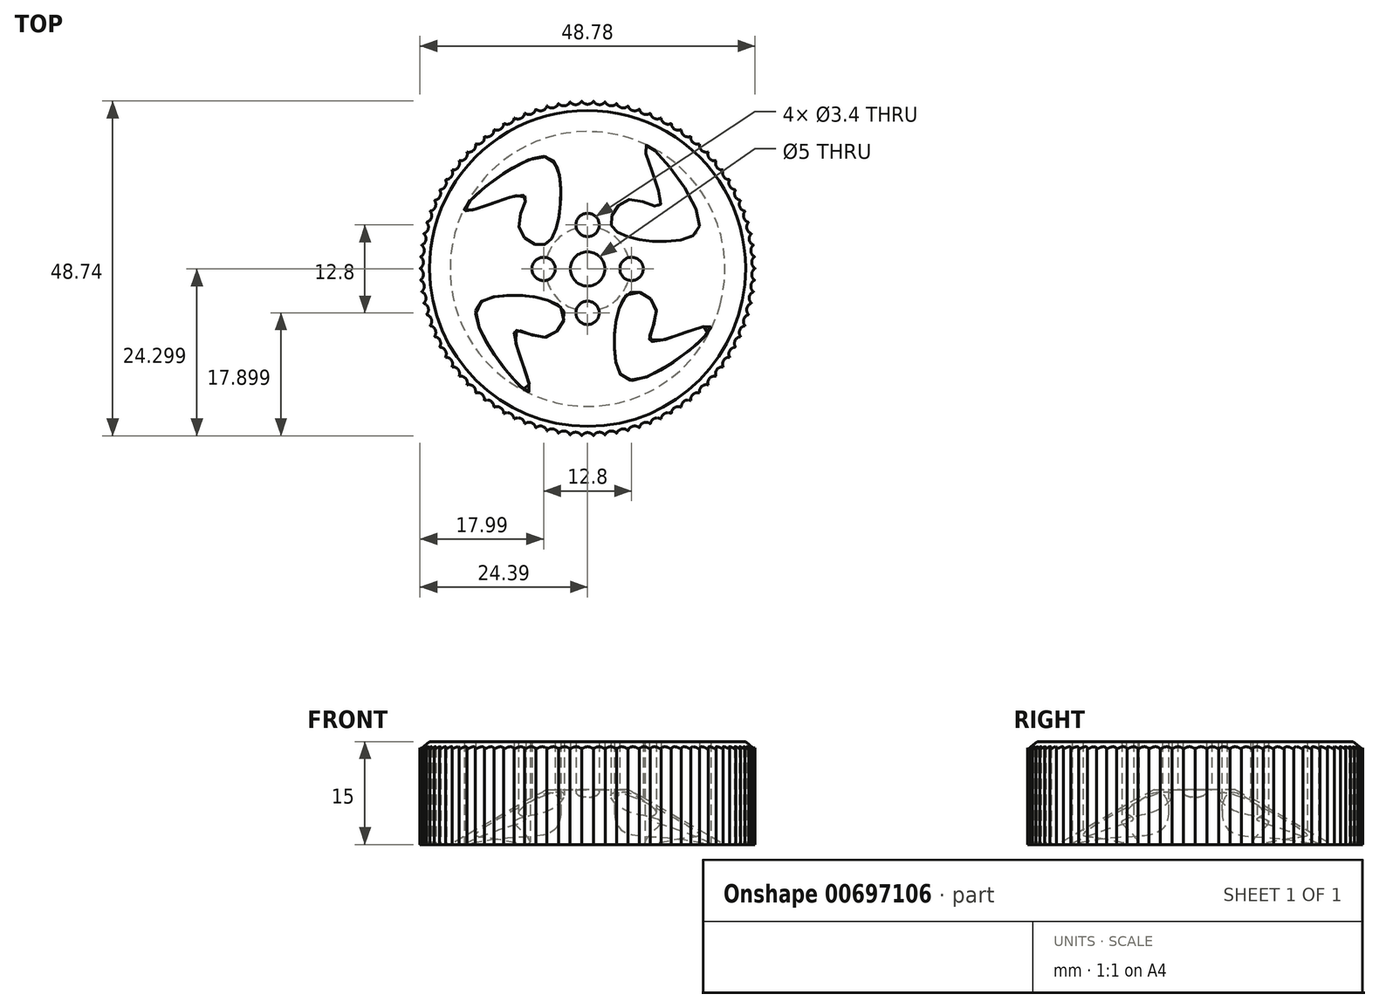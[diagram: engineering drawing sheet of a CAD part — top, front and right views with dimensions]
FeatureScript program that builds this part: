
annotation { "Feature Type Name" : "Feature", "Feature Type Description" : "" }
export const myFeature = defineFeature(function(context is Context, id is Id, definition is map)
    precondition{}
    {
        {
            var Q0;
            Q0=qCreatedBy(makeId("Top.planeOp"),FACE);
            var sketch = newSketch(context, id + "F0", { "sketchPlane" : qUnion([Q0])});
            skCircle(sketch, "E0", {"center": v(0, -0.07) * mm, "radius": 25 * mm});
            skCircle(sketch, "E1", {"center": v(0, -0.07) * mm, "radius": 20 * mm});
            skCircle(sketch, "E2", {"center": v(0, -0.07) * mm, "radius": 2.5 * mm});
            skCircle(sketch, "E3", {"center": v(0, 6.33) * mm, "radius": 1.7 * mm});
            skCircle(sketch, "E4", {"center": v(6.4, -0.07) * mm, "radius": 1.7 * mm});
            skCircle(sketch, "E5", {"center": v(0, -6.47) * mm, "radius": 1.7 * mm});
            skCircle(sketch, "E6", {"center": v(-6.4, -0.07) * mm, "radius": 1.7 * mm});
            skSolve(sketch);
        }
        {
            var Q0;
            Q0=makeQuery(id+"F0.imprint","IMPRINT",FACE,{"disambiguationData":[TD([[makeQuery(id+"F0.imprint","IMPRINT",EDGE,{"derivedFrom":sQuery(id+"F0.wireOp",EDGE,"E0")}),1.0]])]});
            var Q1;
            Q1=makeQuery(id+"F0.imprint","IMPRINT",FACE,{"disambiguationData":[TD([[makeQuery(id+"F0.imprint","IMPRINT",EDGE,{"derivedFrom":sQuery(id+"F0.wireOp",EDGE,"E1")}),1.0]])]});
            extrude(context, id + "F1", {"entities" : qUnion([Q0, Q1]), "depth" : 15 * mm, "offsetDistance" : 25 * mm});
        }
        {
            var Q0;
            Q0=makeQuery(id+"F0.imprint","IMPRINT",FACE,{"disambiguationData":[TD([[makeQuery(id+"F0.imprint","IMPRINT",EDGE,{"derivedFrom":sQuery(id+"F0.wireOp",EDGE,"E1")}),1.0]])]});
            var Q1;
            Q1=makeQuery(id+"F0.imprint","IMPRINT",FACE,{"disambiguationData":[TD([[makeQuery(id+"F0.imprint","IMPRINT",EDGE,{"derivedFrom":sQuery(id+"F0.wireOp",EDGE,"E5")}),1.0]])]});
            var Q2;
            Q2=makeQuery(id+"F0.imprint","IMPRINT",FACE,{"disambiguationData":[TD([[makeQuery(id+"F0.imprint","IMPRINT",EDGE,{"derivedFrom":sQuery(id+"F0.wireOp",EDGE,"E4")}),1.0]])]});
            var Q3;
            Q3=makeQuery(id+"F0.imprint","IMPRINT",FACE,{"disambiguationData":[TD([[makeQuery(id+"F0.imprint","IMPRINT",EDGE,{"derivedFrom":sQuery(id+"F0.wireOp",EDGE,"E2")}),1.0]])]});
            var Q4;
            Q4=makeQuery(id+"F0.imprint","IMPRINT",FACE,{"disambiguationData":[TD([[makeQuery(id+"F0.imprint","IMPRINT",EDGE,{"derivedFrom":sQuery(id+"F0.wireOp",EDGE,"E3")}),1.0]])]});
            var Q5;
            Q5=makeQuery(id+"F0.imprint","IMPRINT",FACE,{"disambiguationData":[TD([[makeQuery(id+"F0.imprint","IMPRINT",EDGE,{"derivedFrom":sQuery(id+"F0.wireOp",EDGE,"E6")}),1.0]])]});
            extrude(context, id + "F2", {"entities" : qUnion([Q0, Q1, Q2, Q3, Q4, Q5]), "operationType" : NewBodyOperationType.REMOVE, "depth" : 8 * mm, "offsetDistance" : 25 * mm, "hasDraft" : true, "draftAngle" : 60 * degree, "draftPullDirection" : true});
        }
        {
            var Q0;
            Q0=qCreatedBy(makeId("Top.planeOp"),FACE);
            var sketch = newSketch(context, id + "F3", { "sketchPlane" : qUnion([Q0])});
            skCircle(sketch, "E7", {"center": v(0, 24.9) * mm, "radius": 1 * mm});
            skSolve(sketch);
        }
        {
            var Q0;
            Q0=makeQuery(id+"F3.imprint","IMPRINT",FACE,{"disambiguationData":[TD([[makeQuery(id+"F3.imprint","IMPRINT",EDGE,{"derivedFrom":sQuery(id+"F3.wireOp",EDGE,"E7")}),1.0]])]});
            extrude(context, id + "F4", {"entities" : qUnion([Q0]), "depth" : 25 * mm, "offsetDistance" : 25 * mm});
        }
        {
            var Q0;
            Q0=qCreatedBy(makeId("Right.planeOp"),FACE);
            var sketch = newSketch(context, id + "F5", { "sketchPlane" : qUnion([Q0])});
            skLineSegment(sketch, "E8", {"start": v(0, 25.16) * mm, "end": v(0, -9.7) * mm});
            skSolve(sketch);
        }
        {
            var Q0;
            Q0=makeQuery(id+"F4.opExtrude","SWEPT_BODY",BODY,{"disambiguationData":[OSD([sQuery(id+"F3.wireOp",EDGE,"E7")])]});
            var Q1;
            Q1=sQuery(id+"F5.wireOp",EDGE,"E8");
            circularPattern(context, id + "F6", {"operationType" : NewBodyOperationType.REMOVE, "entities" : qUnion([Q0]), "axis" : qUnion([Q1]), "angle" : 360 * degree, "instanceCount" : 90, "equalSpace" : true});
        }
        {
            var Q0;
            Q0=makeQuery(id+"F1.opExtrude","CAP_FACE",FACE,{"disambiguationData":[OSD([sQuery(id+"F0.wireOp",EDGE,"E0"),sQuery(id+"F0.wireOp",EDGE,"E2"),sQuery(id+"F0.wireOp",EDGE,"E3"),sQuery(id+"F0.wireOp",EDGE,"E4"),sQuery(id+"F0.wireOp",EDGE,"E5"),sQuery(id+"F0.wireOp",EDGE,"E6")])],"isStart":false});
            var sketch = newSketch(context, id + "F7", { "sketchPlane" : qUnion([Q0])});
            skCircle(sketch, "E9", {"center": v(0, 0) * mm, "radius": 23 * mm});
            skCircle(sketch, "E10", {"center": v(0, 0) * mm, "radius": 25.5 * mm});
            skSolve(sketch);
        }
        {
            var Q0;
            Q0=makeQuery(id+"F7.imprint","IMPRINT",FACE,{"disambiguationData":[TD([[makeQuery(id+"F7.imprint","IMPRINT",EDGE,{"derivedFrom":sQuery(id+"F7.wireOp",EDGE,"E9")}),-1.0]])]});
            var Q1;
            Q1=makeQuery(id+"F7.imprint","IMPRINT",FACE,{"disambiguationData":[TD([[makeQuery(id+"F7.imprint","IMPRINT",EDGE,{"derivedFrom":sQuery(id+"F7.wireOp",EDGE,"E10")}),1.0]])]});
            extrude(context, id + "F8", {"entities" : qUnion([Q0, Q1]), "operationType" : NewBodyOperationType.REMOVE, "oppositeDirection" : true, "depth" : 1.5 * mm, "offsetDistance" : 25 * mm, "hasDraft" : true, "draftAngle" : 50 * degree, "draftPullDirection" : true});
        }
        {
            var Q0;
            Q0=makeQuery(id+"F0.imprint","IMPRINT",FACE,{"disambiguationData":[TD([[makeQuery(id+"F0.imprint","IMPRINT",EDGE,{"derivedFrom":sQuery(id+"F0.wireOp",EDGE,"E0")}),1.0]])]});
            var sketch = newSketch(context, id + "F9", { "sketchPlane" : qUnion([Q0])});
            skFitSpline(sketch, "E11", {"points": [v(-5.8, -4.62) * mm, v(-12.21, -3.95) * mm, v(-16.3, -6.78) * mm, v(-8.43, -17.88) * mm, v(-10.63, -9.24) * mm, v(-6.3, -10.03) * mm, v(-3.38, -6.7) * mm, v(-5.8, -4.62) * mm]});
            skSolve(sketch);
        }
        {
            var Q0;
            Q0=qSketchRegion(id+"F9",true);
            extrude(context, id + "F10", {"entities" : qUnion([Q0]), "depth" : 25 * mm, "offsetDistance" : 25 * mm});
        }
        {
            var Q0;
            Q0=makeQuery(id+"F10.opExtrude","SWEPT_BODY",BODY,{"disambiguationData":[OSD([sQuery(id+"F9.wireOp",EDGE,"E11")])]});
            var Q1;
            Q1=sQuery(id+"F5.wireOp",EDGE,"E8");
            var Q2;
            Q2=makeQuery(id+"F1.opExtrude","SWEPT_BODY",BODY,{"disambiguationData":[OSD([sQuery(id+"F0.wireOp",EDGE,"E0"),sQuery(id+"F0.wireOp",EDGE,"E2"),sQuery(id+"F0.wireOp",EDGE,"E3"),sQuery(id+"F0.wireOp",EDGE,"E4"),sQuery(id+"F0.wireOp",EDGE,"E5"),sQuery(id+"F0.wireOp",EDGE,"E6")])]});
            circularPattern(context, id + "F11", {"operationType" : NewBodyOperationType.REMOVE, "entities" : qUnion([Q0]), "axis" : qUnion([Q1]), "angle" : 360 * degree, "instanceCount" : 4, "equalSpace" : true});
        }
    });
